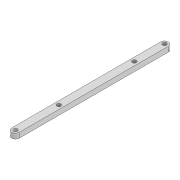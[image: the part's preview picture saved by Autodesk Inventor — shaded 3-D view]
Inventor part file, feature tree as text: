
AUTODESK INVENTOR PART (.ipt)
format: ipt  version: 2022 (Build 260153000, 153)  size: 90,624 bytes
history: native  units: mm
features: extrude x1, sketch x1
ambient origin geometry x8: Origin, YZ Plane, XZ Plane, XY Plane, X Axis, Y Axis, Z Axis, Center Point
bodies: Solid1 (feature_tree)
feature tree (2):
  extrude  "Extrusion1"  Depth=93.045mm
  sketch  "Sketch1"  dims[d0=3.2mm d1=3.2mm d2=6.0mm d3=116.749mm d4=3.2mm d5=33.922mm d6=4.0mm d7=0.0mm d8=3.2mm d9=93.045mm]
